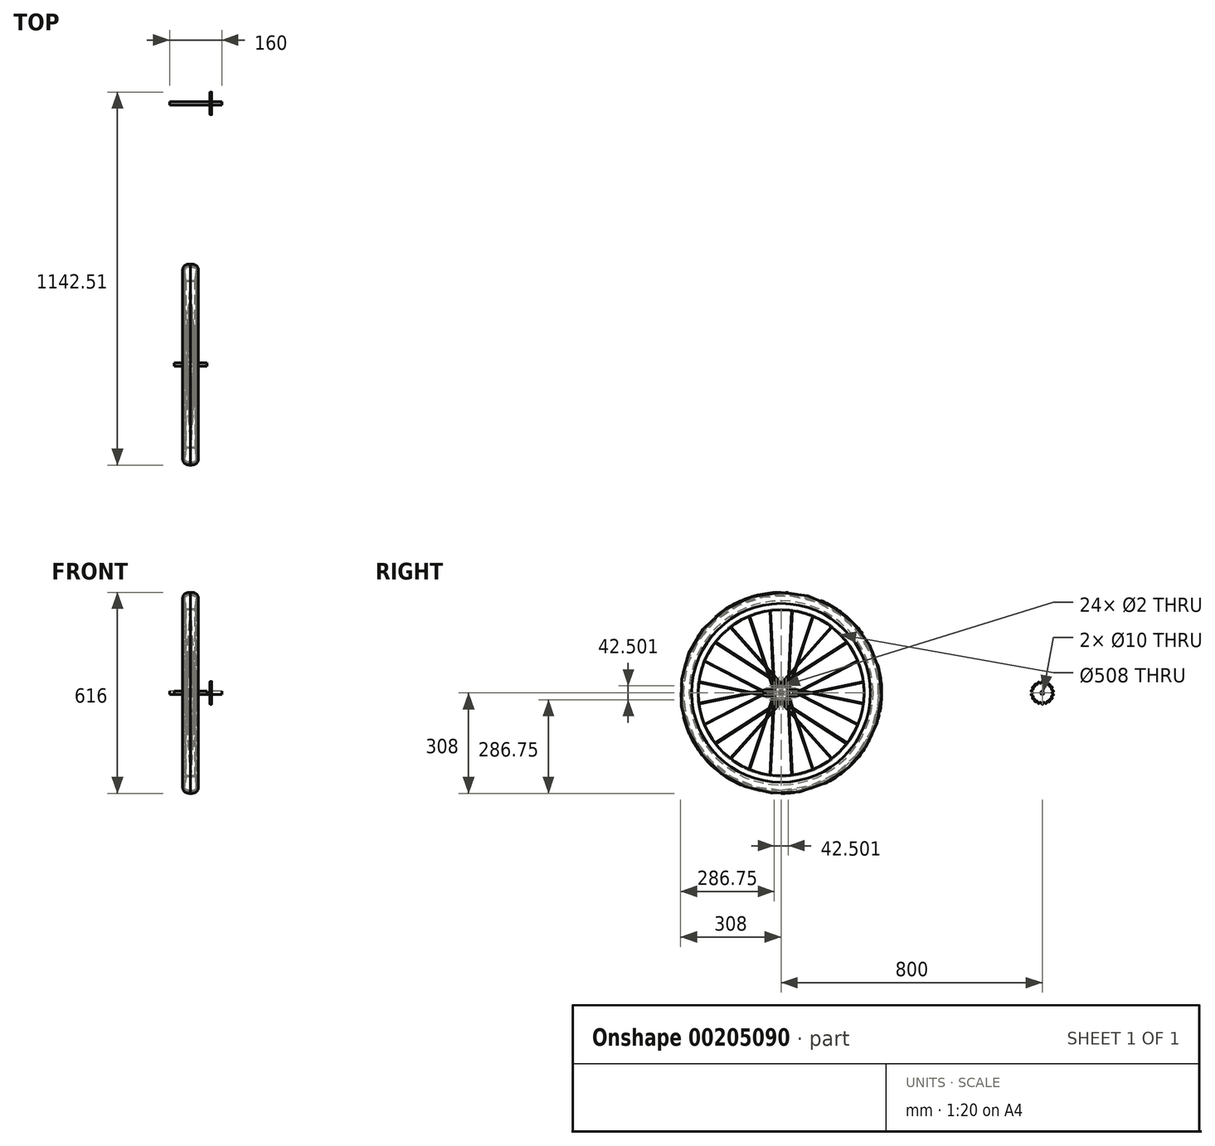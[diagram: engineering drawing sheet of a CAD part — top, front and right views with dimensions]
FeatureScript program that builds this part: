
annotation { "Feature Type Name" : "Feature", "Feature Type Description" : "" }
export const myFeature = defineFeature(function(context is Context, id is Id, definition is map)
    precondition{}
    {
        {
            var Q0;
            Q0=qCreatedBy(makeId("Right.planeOp"),FACE);
            var sketch = newSketch(context, id + "F0", { "sketchPlane" : qUnion([Q0])});
            skCircle(sketch, "E0", {"center": v(0, 0) * mm, "radius": 8 * mm});
            skCircle(sketch, "E1", {"center": v(0, 0) * mm, "radius": 5 * mm});
            skSolve(sketch);
        }
        {
            var Q0;
            Q0 = qSketchRegion(id + "F0", true);
            extrude(context, id + "F1", {"entities" : qUnion([Q0]), "depth" : 15 * mm});
        }
        {
            var Q0;
            Q0=makeQuery(id+"F1.opExtrude","CAP_FACE",FACE,{"disambiguationData":[OSD([sQuery(id+"F0.wireOp",EDGE,"E0"),sQuery(id+"F0.wireOp",EDGE,"E1")])],"isStart":false});
            var sketch = newSketch(context, id + "F2", { "sketchPlane" : qUnion([Q0])});
            skCircle(sketch, "E2", {"center": v(0, 0) * mm, "radius": 25 * mm});
            skCircle(sketch, "E3", {"center": v(0, 0) * mm, "radius": 5 * mm});
            skSolve(sketch);
        }
        {
            var Q0;
            Q0 = qSketchRegion(id + "F2", true);
            extrude(context, id + "F3", {"entities" : qUnion([Q0]), "operationType" : NewBodyOperationType.ADD, "oppositeDirection" : true, "depth" : 2 * mm});
        }
        {
            var Q0;
            Q0=makeQuery(id+"F3.boolean.opBoolean","MERGE",FACE,{"derivedFrom":[makeQuery(id+"F1.opExtrude","CAP_FACE",FACE,{"disambiguationData":[OSD([sQuery(id+"F0.wireOp",EDGE,"E0"),sQuery(id+"F0.wireOp",EDGE,"E1")])],"isStart":false}),makeQuery(id+"F3.opExtrude","CAP_FACE",FACE,{"disambiguationData":[OSD([sQuery(id+"F2.wireOp",EDGE,"E2"),sQuery(id+"F2.wireOp",EDGE,"E3")])],"isStart":true})]});
            var sketch = newSketch(context, id + "F4", { "sketchPlane" : qUnion([Q0])});
            skCircle(sketch, "E4", {"center": v(5.7, 21.25) * mm, "radius": 1 * mm});
            skLineSegment(sketch, "E5", {"start": v(0, 0) * mm, "end": v(5.7, 21.25) * mm, "construction": true});
            skCircle(sketch, "E6.1.0", {"center": v(-5.7, 21.25) * mm, "radius": 1 * mm});
            skCircle(sketch, "E6.2.0", {"center": v(-15.56, 15.56) * mm, "radius": 1 * mm});
            skCircle(sketch, "E6.3.0", {"center": v(-21.25, 5.7) * mm, "radius": 1 * mm});
            skCircle(sketch, "E6.4.0", {"center": v(-21.25, -5.7) * mm, "radius": 1 * mm});
            skCircle(sketch, "E6.5.0", {"center": v(-15.56, -15.56) * mm, "radius": 1 * mm});
            skCircle(sketch, "E6.6.0", {"center": v(-5.7, -21.25) * mm, "radius": 1 * mm});
            skCircle(sketch, "E6.7.0", {"center": v(5.7, -21.25) * mm, "radius": 1 * mm});
            skCircle(sketch, "E6.8.0", {"center": v(15.56, -15.56) * mm, "radius": 1 * mm});
            skCircle(sketch, "E6.9.0", {"center": v(21.25, -5.7) * mm, "radius": 1 * mm});
            skCircle(sketch, "E6.10.0", {"center": v(21.25, 5.7) * mm, "radius": 1 * mm});
            skCircle(sketch, "E6.11.0", {"center": v(15.56, 15.56) * mm, "radius": 1 * mm});
            skPoint(sketch, "E6.center", {"position": v(0, 0) * mm});
            skSolve(sketch);
        }
        {
            var Q0;
            Q0 = qSketchRegion(id + "F4", true);
            extrude(context, id + "F5", {"entities" : qUnion([Q0]), "operationType" : NewBodyOperationType.REMOVE, "endBound" : BoundingType.THROUGH_ALL, "oppositeDirection" : true, "depth" : 25 * mm});
        }
        {
            var Q0;
            Q0=makeQuery(id+"F1.opExtrude","SWEPT_BODY",BODY,{"disambiguationData":[OSD([sQuery(id+"F0.wireOp",EDGE,"E0"),sQuery(id+"F0.wireOp",EDGE,"E1")])]});
            var Q1;
            Q1=makeQuery(id+"F1.opExtrude","CAP_FACE",FACE,{"disambiguationData":[OSD([sQuery(id+"F0.wireOp",EDGE,"E0"),sQuery(id+"F0.wireOp",EDGE,"E1")])],"isStart":true});
            mirror(context, id + "F6", {"operationType" : NewBodyOperationType.ADD, "entities" : qUnion([Q0]), "mirrorPlane" : qUnion([Q1])});
        }
        {
            var Q0;
            Q0=qCreatedBy(makeId("Front.planeOp"),FACE);
            var sketch = newSketch(context, id + "F7", { "sketchPlane" : qUnion([Q0])});
            skLineSegment(sketch, "E7", {"start": v(0, 254) * mm, "end": v(20, 254) * mm});
            skLineSegment(sketch, "E8", {"start": v(20, 254) * mm, "end": v(21.74, 273.92) * mm});
            skLineSegment(sketch, "E9", {"start": v(21.74, 273.92) * mm, "end": v(18.75, 274.19) * mm});
            skLineSegment(sketch, "E10", {"start": v(18.75, 274.19) * mm, "end": v(17.25, 257) * mm});
            skLineSegment(sketch, "E11", {"start": v(17.25, 257) * mm, "end": v(0, 257) * mm});
            skLineSegment(sketch, "E12", {"start": v(0, 257) * mm, "end": v(0, 254) * mm, "construction": true});
            skLineSegment(sketch, "E13.MirrorCS", {"start": v(0, 254) * mm, "end": v(-20, 254) * mm});
            skLineSegment(sketch, "E14.MirrorCS", {"start": v(-20, 254) * mm, "end": v(-21.74, 273.92) * mm});
            skLineSegment(sketch, "E15.MirrorCS", {"start": v(-21.74, 273.92) * mm, "end": v(-18.75, 274.19) * mm});
            skLineSegment(sketch, "E16.MirrorCS", {"start": v(-18.75, 274.19) * mm, "end": v(-17.25, 257) * mm});
            skLineSegment(sketch, "E17.MirrorCS", {"start": v(-17.25, 257) * mm, "end": v(0, 257) * mm});
            skSolve(sketch);
        }
        {
            var Q0;
            Q0 = qSketchRegion(id + "F7", true);
            var Q1;
            Q1=makeQuery(id+"F3.opExtrude","CAP_EDGE",EDGE,{"disambiguationData":[OSD([sQuery(id+"F2.wireOp",EDGE,"E2")])],"isStart":false});
            revolve(context, id + "F8", {"entities" : qUnion([Q0]), "axis" : qUnion([Q1]), "revolveType" : RevolveType.FULL});
        }
        {
            var Q0;
            Q0=qCreatedBy(makeId("Right.planeOp"),FACE);
            var sketch = newSketch(context, id + "F9", { "sketchPlane" : qUnion([Q0])});
            skPoint(sketch, "E18", {"position": v(33.28, 252.82) * mm});
            skPoint(sketch, "E19.1.0", {"position": v(-33.28, 252.82) * mm});
            skPoint(sketch, "E19.2.0", {"position": v(-97.58, 235.59) * mm});
            skPoint(sketch, "E19.3.0", {"position": v(-155.23, 202.3) * mm});
            skPoint(sketch, "E19.4.0", {"position": v(-202.3, 155.23) * mm});
            skPoint(sketch, "E19.5.0", {"position": v(-235.59, 97.58) * mm});
            skPoint(sketch, "E19.6.0", {"position": v(-252.82, 33.28) * mm});
            skPoint(sketch, "E19.7.0", {"position": v(-252.82, -33.28) * mm});
            skPoint(sketch, "E19.8.0", {"position": v(-235.59, -97.58) * mm});
            skPoint(sketch, "E19.9.0", {"position": v(-202.3, -155.23) * mm});
            skPoint(sketch, "E19.10.0", {"position": v(-155.23, -202.3) * mm});
            skPoint(sketch, "E19.11.0", {"position": v(-97.58, -235.59) * mm});
            skPoint(sketch, "E19.12.0", {"position": v(-33.28, -252.82) * mm});
            skPoint(sketch, "E19.13.0", {"position": v(33.28, -252.82) * mm});
            skPoint(sketch, "E19.14.0", {"position": v(97.58, -235.59) * mm});
            skPoint(sketch, "E19.15.0", {"position": v(155.23, -202.3) * mm});
            skPoint(sketch, "E19.16.0", {"position": v(202.3, -155.23) * mm});
            skPoint(sketch, "E19.17.0", {"position": v(235.59, -97.58) * mm});
            skPoint(sketch, "E19.18.0", {"position": v(252.82, -33.28) * mm});
            skPoint(sketch, "E19.19.0", {"position": v(252.82, 33.28) * mm});
            skPoint(sketch, "E19.20.0", {"position": v(235.59, 97.58) * mm});
            skPoint(sketch, "E19.21.0", {"position": v(202.3, 155.23) * mm});
            skPoint(sketch, "E19.22.0", {"position": v(155.23, 202.3) * mm});
            skPoint(sketch, "E19.23.0", {"position": v(97.58, 235.59) * mm});
            skPoint(sketch, "E19.center", {"position": v(0, 0) * mm});
            skLineSegment(sketch, "E20", {"start": v(-33.28, 252.82) * mm, "end": v(-21.25, 5.7) * mm, "construction": true});
            skLineSegment(sketch, "E21", {"start": v(0, 0) * mm, "end": v(3.26, 24.79) * mm, "construction": true});
            skLineSegment(sketch, "E22", {"start": v(-15.56, 15.56) * mm, "end": v(-252.82, -33.28) * mm, "construction": true});
            skLineSegment(sketch, "E23", {"start": v(-21.25, 5.7) * mm, "end": v(-97.58, 235.59) * mm, "construction": true});
            skLineSegment(sketch, "E24", {"start": v(-15.56, 15.56) * mm, "end": v(-235.59, -97.58) * mm, "construction": true});
            skLineSegment(sketch, "E25.1.0", {"start": v(-235.59, 97.58) * mm, "end": v(-15.56, -15.56) * mm, "construction": true});
            skLineSegment(sketch, "E25.1.1", {"start": v(-15.56, -15.56) * mm, "end": v(-252.82, 33.28) * mm, "construction": true});
            skLineSegment(sketch, "E25.1.2", {"start": v(-21.25, -5.7) * mm, "end": v(-97.58, -235.59) * mm, "construction": true});
            skLineSegment(sketch, "E25.1.3", {"start": v(-21.25, -5.7) * mm, "end": v(-33.28, -252.82) * mm, "construction": true});
            skLineSegment(sketch, "E25.2.0", {"start": v(-202.3, -155.23) * mm, "end": v(5.7, -21.25) * mm, "construction": true});
            skLineSegment(sketch, "E25.2.1", {"start": v(5.7, -21.25) * mm, "end": v(-155.23, -202.3) * mm, "construction": true});
            skLineSegment(sketch, "E25.2.2", {"start": v(-5.7, -21.25) * mm, "end": v(155.23, -202.3) * mm, "construction": true});
            skLineSegment(sketch, "E25.2.3", {"start": v(-5.7, -21.25) * mm, "end": v(202.3, -155.23) * mm, "construction": true});
            skLineSegment(sketch, "E25.3.0", {"start": v(33.28, -252.82) * mm, "end": v(21.25, -5.7) * mm, "construction": true});
            skLineSegment(sketch, "E25.3.1", {"start": v(21.25, -5.7) * mm, "end": v(97.58, -235.59) * mm, "construction": true});
            skLineSegment(sketch, "E25.3.2", {"start": v(15.56, -15.56) * mm, "end": v(252.82, 33.28) * mm, "construction": true});
            skLineSegment(sketch, "E25.3.3", {"start": v(15.56, -15.56) * mm, "end": v(235.59, 97.58) * mm, "construction": true});
            skLineSegment(sketch, "E25.4.0", {"start": v(235.59, -97.58) * mm, "end": v(15.56, 15.56) * mm, "construction": true});
            skLineSegment(sketch, "E25.4.1", {"start": v(15.56, 15.56) * mm, "end": v(252.82, -33.28) * mm, "construction": true});
            skLineSegment(sketch, "E25.4.2", {"start": v(21.25, 5.7) * mm, "end": v(97.58, 235.59) * mm, "construction": true});
            skLineSegment(sketch, "E25.4.3", {"start": v(21.25, 5.7) * mm, "end": v(33.28, 252.82) * mm, "construction": true});
            skLineSegment(sketch, "E25.5.0", {"start": v(202.3, 155.23) * mm, "end": v(-5.7, 21.25) * mm, "construction": true});
            skLineSegment(sketch, "E25.5.1", {"start": v(-5.7, 21.25) * mm, "end": v(155.23, 202.3) * mm, "construction": true});
            skLineSegment(sketch, "E25.5.2", {"start": v(5.7, 21.25) * mm, "end": v(-155.23, 202.3) * mm, "construction": true});
            skLineSegment(sketch, "E25.5.3", {"start": v(5.7, 21.25) * mm, "end": v(-202.3, 155.23) * mm, "construction": true});
            skSolve(sketch);
        }
        {
            var Q0;
            Q0=sQuery(id+"F9.wireOp",EDGE,"E20");
            cPlane(context, id + "F10", {"entities" : qUnion([Q0]), "cplaneType" : CPlaneType.LINE_ANGLE, "offset" : 25 * mm, "angle" : 90 * degree, "width" : 150 * mm, "height" : 150 * mm});
        }
        {
            var Q0;
            Q0=qCreatedBy(id+"F10.planeOp",FACE);
            var sketch = newSketch(context, id + "F11", { "sketchPlane" : qUnion([Q0])});
            skLineSegment(sketch, "E26", {"start": v(0, 254.14) * mm, "end": v(-17.5, 8.33) * mm});
            skLineSegment(sketch, "E27", {"start": v(-12, 6.72) * mm, "end": v(-16, 6.72) * mm});
            skArc(sketch, "E28", {"start": v(-16, 6.72) * mm, "mid": v(-17.1, 7.2) * mm, "end": v(-17.5, 8.33) * mm});
            skSolve(sketch);
        }
        {
            var Q0;
            Q0=sQuery(id+"F11.wireOp",VERTEX,"E27.start");
            var Q1;
            Q1=sQuery(id+"F11.wireOp",EDGE,"E27");
            cPlane(context, id + "F12", {"entities" : qUnion([Q0, Q1]), "cplaneType" : CPlaneType.CURVE_POINT, "offset" : 25 * mm, "width" : 150 * mm, "height" : 150 * mm});
        }
        {
            var Q0;
            Q0=qCreatedBy(id+"F12.planeOp",FACE);
            var sketch = newSketch(context, id + "F13", { "sketchPlane" : qUnion([Q0])});
            skCircle(sketch, "E29", {"center": v(-21.25, 5.7) * mm, "radius": 1 * mm});
            skSolve(sketch);
        }
        {
            var Q0;
            Q0=makeQuery(id+"F13.imprint","IMPRINT",FACE,{"disambiguationData":[TD([[makeQuery(id+"F13.imprint","IMPRINT",EDGE,{"derivedFrom":sQuery(id+"F13.wireOp",EDGE,"E29")}),1.0]])]});
            var Q1;
            Q1=sQuery(id+"F11.wireOp",EDGE,"E28");
            var Q2;
            Q2=sQuery(id+"F11.wireOp",EDGE,"E27");
            var Q3;
            Q3=sQuery(id+"F11.wireOp",EDGE,"E26");
            sweep(context, id + "F14", {"profiles" : qUnion([Q0]), "path" : qUnion([Q1, Q2, Q3])});
        }
        {
            var Q0;
            Q0=sQuery(id+"F9.wireOp",EDGE,"E22");
            cPlane(context, id + "F15", {"entities" : qUnion([Q0]), "cplaneType" : CPlaneType.LINE_ANGLE, "offset" : 25 * mm, "angle" : 0 * degree, "width" : 150 * mm, "height" : 150 * mm});
        }
        {
            var Q0;
            Q0=qCreatedBy(id+"F15.planeOp",FACE);
            var sketch = newSketch(context, id + "F16", { "sketchPlane" : qUnion([Q0])});
            skLineSegment(sketch, "E30", {"start": v(0, 254.34) * mm, "end": v(10, 13.54) * mm});
            skLineSegment(sketch, "E31", {"start": v(11.5, 12.1) * mm, "end": v(16, 12.1) * mm});
            skArc(sketch, "E32", {"start": v(11.5, 12.1) * mm, "mid": v(10.46, 12.52) * mm, "end": v(10, 13.54) * mm});
            skSolve(sketch);
        }
        {
            var Q0;
            Q0=sQuery(id+"F16.wireOp",EDGE,"E31");
            var Q1;
            Q1=sQuery(id+"F16.wireOp",VERTEX,"E31.end");
            cPlane(context, id + "F17", {"entities" : qUnion([Q0, Q1]), "cplaneType" : CPlaneType.CURVE_POINT, "offset" : 25 * mm, "width" : 150 * mm, "height" : 150 * mm});
        }
        {
            var Q0;
            Q0=qCreatedBy(id+"F17.planeOp",FACE);
            var sketch = newSketch(context, id + "F18", { "sketchPlane" : qUnion([Q0])});
            skCircle(sketch, "E33", {"center": v(-15.56, 15.56) * mm, "radius": 1 * mm});
            skSolve(sketch);
        }
        {
            var Q0;
            Q0=makeQuery(id+"F18.imprint","IMPRINT",FACE,{"disambiguationData":[TD([[makeQuery(id+"F18.imprint","IMPRINT",EDGE,{"derivedFrom":sQuery(id+"F18.wireOp",EDGE,"E33")}),1.0]])]});
            var Q1;
            Q1=sQuery(id+"F16.wireOp",EDGE,"E31");
            var Q2;
            Q2=sQuery(id+"F16.wireOp",EDGE,"E32");
            var Q3;
            Q3=sQuery(id+"F16.wireOp",EDGE,"E30");
            sweep(context, id + "F19", {"profiles" : qUnion([Q0]), "path" : qUnion([Q1, Q2, Q3])});
        }
        {
            var Q0;
            Q0=makeQuery(id+"F14.opSweep","SWEPT_BODY",BODY,{"disambiguationData":[OSD([sQuery(id+"F11.wireOp",EDGE,"E27"),sQuery(id+"F13.wireOp",EDGE,"E29")])]});
            var Q1;
            Q1=makeQuery(id+"F19.opSweep","SWEPT_BODY",BODY,{"disambiguationData":[OSD([sQuery(id+"F16.wireOp",EDGE,"E30"),sQuery(id+"F18.wireOp",EDGE,"E33")])]});
            var Q2;
            Q2=makeQuery(id+"F3.opExtrude","CAP_EDGE",EDGE,{"disambiguationData":[OSD([sQuery(id+"F2.wireOp",EDGE,"E2")])],"isStart":true});
            circularPattern(context, id + "F20", {"entities" : qUnion([Q0, Q1]), "axis" : qUnion([Q2]), "angle" : 360 * degree, "instanceCount" : 6, "equalSpace" : true});
        }
        {
            var Q0;
            Q0=qCreatedBy(makeId("Right.planeOp"),FACE);
            var sketch = newSketch(context, id + "F21", { "sketchPlane" : qUnion([Q0])});
            skLineSegment(sketch, "E34", {"start": v(0, 0) * mm, "end": v(0, 5) * mm, "construction": true});
            skSolve(sketch);
        }
        {
            var Q0;
            Q0=makeQuery(id+"F14.opSweep","SWEPT_BODY",BODY,{"disambiguationData":[OSD([sQuery(id+"F11.wireOp",EDGE,"E27"),sQuery(id+"F13.wireOp",EDGE,"E29")])]});
            var Q1;
            Q1=makeQuery(id+"F19.opSweep","SWEPT_BODY",BODY,{"disambiguationData":[OSD([sQuery(id+"F16.wireOp",EDGE,"E30"),sQuery(id+"F18.wireOp",EDGE,"E33")])]});
            var Q2;
            Q2=makeQuery(id+"F20.opPattern","COPY",BODY,{"derivedFrom":makeQuery(id+"F14.opSweep","SWEPT_BODY",BODY,{"disambiguationData":[OSD([sQuery(id+"F11.wireOp",EDGE,"E27"),sQuery(id+"F13.wireOp",EDGE,"E29")])]}),"instanceName":"1"});
            var Q3;
            Q3=makeQuery(id+"F20.opPattern","COPY",BODY,{"derivedFrom":makeQuery(id+"F19.opSweep","SWEPT_BODY",BODY,{"disambiguationData":[OSD([sQuery(id+"F16.wireOp",EDGE,"E30"),sQuery(id+"F18.wireOp",EDGE,"E33")])]}),"instanceName":"1"});
            var Q4;
            Q4=makeQuery(id+"F20.opPattern","COPY",BODY,{"derivedFrom":makeQuery(id+"F14.opSweep","SWEPT_BODY",BODY,{"disambiguationData":[OSD([sQuery(id+"F11.wireOp",EDGE,"E27"),sQuery(id+"F13.wireOp",EDGE,"E29")])]}),"instanceName":"2"});
            var Q5;
            Q5=makeQuery(id+"F20.opPattern","COPY",BODY,{"derivedFrom":makeQuery(id+"F19.opSweep","SWEPT_BODY",BODY,{"disambiguationData":[OSD([sQuery(id+"F16.wireOp",EDGE,"E30"),sQuery(id+"F18.wireOp",EDGE,"E33")])]}),"instanceName":"2"});
            var Q6;
            Q6=makeQuery(id+"F20.opPattern","COPY",BODY,{"derivedFrom":makeQuery(id+"F14.opSweep","SWEPT_BODY",BODY,{"disambiguationData":[OSD([sQuery(id+"F11.wireOp",EDGE,"E27"),sQuery(id+"F13.wireOp",EDGE,"E29")])]}),"instanceName":"3"});
            var Q7;
            Q7=makeQuery(id+"F20.opPattern","COPY",BODY,{"derivedFrom":makeQuery(id+"F19.opSweep","SWEPT_BODY",BODY,{"disambiguationData":[OSD([sQuery(id+"F16.wireOp",EDGE,"E30"),sQuery(id+"F18.wireOp",EDGE,"E33")])]}),"instanceName":"3"});
            var Q8;
            Q8=makeQuery(id+"F20.opPattern","COPY",BODY,{"derivedFrom":makeQuery(id+"F14.opSweep","SWEPT_BODY",BODY,{"disambiguationData":[OSD([sQuery(id+"F11.wireOp",EDGE,"E27"),sQuery(id+"F13.wireOp",EDGE,"E29")])]}),"instanceName":"4"});
            var Q9;
            Q9=makeQuery(id+"F20.opPattern","COPY",BODY,{"derivedFrom":makeQuery(id+"F19.opSweep","SWEPT_BODY",BODY,{"disambiguationData":[OSD([sQuery(id+"F16.wireOp",EDGE,"E30"),sQuery(id+"F18.wireOp",EDGE,"E33")])]}),"instanceName":"4"});
            var Q10;
            Q10=makeQuery(id+"F20.opPattern","COPY",BODY,{"derivedFrom":makeQuery(id+"F14.opSweep","SWEPT_BODY",BODY,{"disambiguationData":[OSD([sQuery(id+"F11.wireOp",EDGE,"E27"),sQuery(id+"F13.wireOp",EDGE,"E29")])]}),"instanceName":"5"});
            var Q11;
            Q11=makeQuery(id+"F20.opPattern","COPY",BODY,{"derivedFrom":makeQuery(id+"F19.opSweep","SWEPT_BODY",BODY,{"disambiguationData":[OSD([sQuery(id+"F16.wireOp",EDGE,"E30"),sQuery(id+"F18.wireOp",EDGE,"E33")])]}),"instanceName":"5"});
            var Q12;
            Q12=sQuery(id+"F21.wireOp",EDGE,"E34");
            circularPattern(context, id + "F22", {"entities" : qUnion([Q0, Q1, Q2, Q3, Q4, Q5, Q6, Q7, Q8, Q9, Q10, Q11]), "axis" : qUnion([Q12]), "angle" : 360 * degree, "instanceCount" : 2, "equalSpace" : true});
        }
        {
            var Q0;
            Q0=qCreatedBy(makeId("Right.planeOp"),FACE);
            var sketch = newSketch(context, id + "F23", { "sketchPlane" : qUnion([Q0])});
            skCircle(sketch, "E35.0", {"center": v(0, 0) * mm, "radius": 5 * mm});
            skSolve(sketch);
        }
        {
            var Q0;
            Q0 = qSketchRegion(id + "F23", true);
            extrude(context, id + "F24", {"entities" : qUnion([Q0]), "depth" : 50 * mm, "hasSecondDirection" : true, "secondDirectionOppositeDirection" : true, "secondDirectionDepth" : 50 * mm});
        }
        {
            var Q0;
            Q0=qCreatedBy(makeId("Front.planeOp"),FACE);
            var sketch = newSketch(context, id + "F25", { "sketchPlane" : qUnion([Q0])});
            skFitSpline(sketch, "E36", {"points": [v(0, 302) * mm, v(-18, 296) * mm, v(-21, 286) * mm, v(-18.75, 274.19) * mm], "startDerivative": vector(-76.14, 0) * mm, "endDerivative": vector(3.33, -38.1) * mm});
            skFitSpline(sketch, "E37.MirrorCS", {"points": [v(0, 302) * mm, v(18, 296) * mm, v(21, 286) * mm, v(18.75, 274.19) * mm], "startDerivative": vector(76.14, 0) * mm, "endDerivative": vector(-3.33, -38.1) * mm});
            skLineSegment(sketch, "E38", {"start": v(-18.75, 274.19) * mm, "end": v(-17.25, 257) * mm});
            skLineSegment(sketch, "E39.MirrorCS", {"start": v(18.75, 274.19) * mm, "end": v(17.25, 257) * mm});
            skLineSegment(sketch, "E40.0", {"start": v(-15.77, 274.45) * mm, "end": v(-14.24, 257) * mm});
            skFitSpline(sketch, "E40.1", {"points": [v(0, 299) * mm, v(-3.03, 299) * mm, v(-6.77, 298.67) * mm, v(-10.38, 297.74) * mm, v(-12.47, 296.84) * mm, v(-14.08, 295.8) * mm, v(-15.34, 294.59) * mm, v(-16.38, 293.17) * mm, v(-17.18, 291.58) * mm, v(-17.64, 290.14) * mm, v(-17.88, 288.94) * mm, v(-18, 288.02) * mm, v(-18.03, 287.24) * mm, v(-18.03, 286.61) * mm, v(-18, 285.99) * mm, v(-17.92, 285.18) * mm, v(-17.76, 284.16) * mm, v(-17.55, 283.1) * mm, v(-17.2, 281.61) * mm, v(-16.7, 279.66) * mm, v(-16.12, 277.16) * mm, v(-15.85, 275.37) * mm, v(-15.77, 274.45) * mm]});
            skFitSpline(sketch, "E40.2", {"points": [v(0, 299) * mm, v(3.03, 299) * mm, v(6.77, 298.67) * mm, v(10.38, 297.74) * mm, v(12.47, 296.84) * mm, v(14.08, 295.8) * mm, v(15.34, 294.59) * mm, v(16.38, 293.17) * mm, v(17.18, 291.58) * mm, v(17.64, 290.14) * mm, v(17.88, 288.94) * mm, v(18, 288.02) * mm, v(18.03, 287.24) * mm, v(18.03, 286.61) * mm, v(18, 285.99) * mm, v(17.92, 285.18) * mm, v(17.76, 284.16) * mm, v(17.55, 283.1) * mm, v(17.2, 281.61) * mm, v(16.7, 279.66) * mm, v(16.12, 277.16) * mm, v(15.85, 275.37) * mm, v(15.77, 274.45) * mm]});
            skLineSegment(sketch, "E40.3", {"start": v(15.77, 274.45) * mm, "end": v(14.24, 257) * mm});
            skLineSegment(sketch, "E41", {"start": v(-17.25, 257) * mm, "end": v(-14.24, 257) * mm});
            skLineSegment(sketch, "E42", {"start": v(17.25, 257) * mm, "end": v(14.24, 257) * mm});
            skSolve(sketch);
        }
        {
            var Q0;
            Q0 = qSketchRegion(id + "F25", true);
            var Q1;
            Q1=makeQuery(id+"F8.opRevolve","SWEPT_EDGE",EDGE,{"disambiguationData":[OSD([sQuery(id+"F7.wireOp",EDGE,"E14.MirrorCS"),sQuery(id+"F7.wireOp",EDGE,"E15.MirrorCS")])]});
            revolve(context, id + "F26", {"entities" : qUnion([Q0]), "axis" : qUnion([Q1]), "revolveType" : RevolveType.FULL});
        }
        {
            var Q0;
            Q0=qCreatedBy(makeId("Front.planeOp"),FACE);
            var sketch = newSketch(context, id + "F27", { "sketchPlane" : qUnion([Q0])});
            skFitSpline(sketch, "E43.0", {"points": [v(0, 308) * mm, v(-1.72, 308) * mm, v(-4.92, 307.86) * mm, v(-9.07, 307.26) * mm, v(-12.64, 306.27) * mm, v(-15.68, 304.9) * mm, v(-17.8, 303.44) * mm, v(-19.24, 302.13) * mm, v(-20.2, 301.08) * mm, v(-21.04, 299.98) * mm, v(-22.04, 298.42) * mm, v(-23.01, 296.32) * mm, v(-23.62, 294.05) * mm, v(-23.9, 292.16) * mm, v(-24, 290.7) * mm, v(-24.02, 289.2) * mm, v(-23.92, 287.15) * mm, v(-23.6, 284.59) * mm, v(-23.07, 281.55) * mm, v(-22.5, 278.65) * mm, v(-22, 276.02) * mm, v(-21.8, 274.55) * mm, v(-21.74, 273.92) * mm]});
            skFitSpline(sketch, "E43.1", {"points": [v(0, 308) * mm, v(1.72, 308) * mm, v(4.92, 307.86) * mm, v(9.07, 307.26) * mm, v(12.64, 306.27) * mm, v(15.68, 304.9) * mm, v(17.8, 303.44) * mm, v(19.24, 302.13) * mm, v(20.2, 301.08) * mm, v(21.04, 299.98) * mm, v(22.04, 298.42) * mm, v(23.01, 296.32) * mm, v(23.62, 294.05) * mm, v(23.9, 292.16) * mm, v(24, 290.7) * mm, v(24.02, 289.2) * mm, v(23.92, 287.15) * mm, v(23.6, 284.59) * mm, v(23.07, 281.55) * mm, v(22.5, 278.65) * mm, v(22, 276.02) * mm, v(21.8, 274.55) * mm, v(21.74, 273.92) * mm]});
            skFitSpline(sketch, "E44.0", {"points": [v(0, 305) * mm, v(-10, 305) * mm, v(-18.86, 300.78) * mm, v(-22.3, 289.12) * mm, v(-19.1, 278.17) * mm, v(-18.75, 274.19) * mm]});
            skFitSpline(sketch, "E45.0", {"points": [v(0, 305) * mm, v(10, 305) * mm, v(18.86, 300.78) * mm, v(22.3, 289.12) * mm, v(19.1, 278.17) * mm, v(18.75, 274.19) * mm]});
            skLineSegment(sketch, "E46", {"start": v(-21.74, 273.92) * mm, "end": v(-18.75, 274.19) * mm});
            skLineSegment(sketch, "E47", {"start": v(18.75, 274.19) * mm, "end": v(21.74, 273.92) * mm});
            skSolve(sketch);
        }
        {
            var Q0;
            Q0 = qSketchRegion(id + "F27", true);
            var Q1;
            Q1=makeQuery(id+"F8.opRevolve","SWEPT_EDGE",EDGE,{"disambiguationData":[OSD([sQuery(id+"F7.wireOp",EDGE,"E8"),sQuery(id+"F7.wireOp",EDGE,"E9")])]});
            revolve(context, id + "F28", {"operationType" : NewBodyOperationType.ADD, "entities" : qUnion([Q0]), "axis" : qUnion([Q1]), "revolveType" : RevolveType.FULL});
        }
        {
            var Q0;
            Q0=qCreatedBy(id+"F17.planeOp",FACE);
            var sketch = newSketch(context, id + "F29", { "sketchPlane" : qUnion([Q0])});
            skCircle(sketch, "E48", {"center": v(800, 0) * mm, "radius": 5 * mm});
            skSolve(sketch);
        }
        {
            var Q0;
            Q0 = qSketchRegion(id + "F29", true);
            extrude(context, id + "F30", {"entities" : qUnion([Q0]), "depth" : 80 * mm, "hasSecondDirection" : true, "secondDirectionOppositeDirection" : true, "secondDirectionDepth" : 80 * mm});
        }
        {
            var Q0;
            Q0=qCreatedBy(makeId("Right.planeOp"),FACE);
            cPlane(context, id + "F31", {"entities" : qUnion([Q0]), "cplaneType" : CPlaneType.OFFSET, "offset" : 60 * mm, "width" : 150 * mm, "height" : 150 * mm});
        }
        {
            var Q0;
            Q0=qCreatedBy(id+"F31.planeOp",FACE);
            var sketch = newSketch(context, id + "F32", { "sketchPlane" : qUnion([Q0])});
            skCircle(sketch, "E49.0", {"center": v(800, 0) * mm, "radius": 5 * mm});
            skCircle(sketch, "E50", {"center": v(800, 0) * mm, "radius": 30 * mm});
            skLineSegment(sketch, "E51", {"start": v(800, 0) * mm, "end": v(800, 30) * mm, "construction": true});
            skArc(sketch, "E52", {"start": v(802.5, 32.5) * mm, "mid": v(803.2, 30.6) * mm, "end": v(804.97, 29.59) * mm});
            skArc(sketch, "E53", {"start": v(802.5, 32.5) * mm, "mid": v(801.77, 34.27) * mm, "end": v(800, 35) * mm});
            skArc(sketch, "E54.MirrorCS", {"start": v(797.5, 32.5) * mm, "mid": v(798.23, 34.27) * mm, "end": v(800, 35) * mm});
            skArc(sketch, "E55.MirrorCS", {"start": v(797.5, 32.5) * mm, "mid": v(796.8, 30.6) * mm, "end": v(795.03, 29.59) * mm});
            skArc(sketch, "E56.1.0", {"start": v(791.23, 31.4) * mm, "mid": v(789.94, 32.8) * mm, "end": v(788.03, 32.89) * mm});
            skArc(sketch, "E56.1.1", {"start": v(786.54, 29.68) * mm, "mid": v(786.62, 31.6) * mm, "end": v(788.03, 32.89) * mm});
            skArc(sketch, "E56.1.2", {"start": v(786.54, 29.68) * mm, "mid": v(786.53, 27.65) * mm, "end": v(785.21, 26.1) * mm});
            skArc(sketch, "E56.1.3", {"start": v(791.23, 31.4) * mm, "mid": v(792.54, 29.84) * mm, "end": v(794.55, 29.5) * mm});
            skArc(sketch, "E56.2.0", {"start": v(781.02, 26.5) * mm, "mid": v(779.33, 27.39) * mm, "end": v(777.5, 26.81) * mm});
            skArc(sketch, "E56.2.1", {"start": v(777.2, 23.29) * mm, "mid": v(776.62, 25.11) * mm, "end": v(777.5, 26.81) * mm});
            skArc(sketch, "E56.2.2", {"start": v(777.2, 23.29) * mm, "mid": v(777.89, 21.38) * mm, "end": v(777.18, 19.47) * mm});
            skArc(sketch, "E56.2.3", {"start": v(781.02, 26.5) * mm, "mid": v(782.79, 25.5) * mm, "end": v(784.79, 25.86) * mm});
            skArc(sketch, "E56.3.0", {"start": v(773.1, 18.42) * mm, "mid": v(771.2, 18.66) * mm, "end": v(769.69, 17.5) * mm});
            skArc(sketch, "E56.3.1", {"start": v(770.6, 14.08) * mm, "mid": v(769.44, 15.6) * mm, "end": v(769.69, 17.5) * mm});
            skArc(sketch, "E56.3.2", {"start": v(770.6, 14.08) * mm, "mid": v(771.9, 12.53) * mm, "end": v(771.9, 10.5) * mm});
            skArc(sketch, "E56.3.3", {"start": v(773.1, 18.42) * mm, "mid": v(775.1, 18.07) * mm, "end": v(776.86, 19.1) * mm});
            skArc(sketch, "E56.4.0", {"start": v(768.43, 8.1) * mm, "mid": v(766.56, 7.7) * mm, "end": v(765.53, 6.08) * mm});
            skArc(sketch, "E56.4.1", {"start": v(767.56, 3.18) * mm, "mid": v(765.95, 4.2) * mm, "end": v(765.53, 6.08) * mm});
            skArc(sketch, "E56.4.2", {"start": v(767.56, 3.18) * mm, "mid": v(769.32, 2.16) * mm, "end": v(770, 0.25) * mm});
            skArc(sketch, "E56.4.3", {"start": v(768.43, 8.1) * mm, "mid": v(770.43, 8.46) * mm, "end": v(771.73, 10.03) * mm});
            skArc(sketch, "E56.5.0", {"start": v(767.56, -3.18) * mm, "mid": v(765.95, -4.2) * mm, "end": v(765.53, -6.08) * mm});
            skArc(sketch, "E56.5.1", {"start": v(768.43, -8.1) * mm, "mid": v(766.56, -7.7) * mm, "end": v(765.53, -6.08) * mm});
            skArc(sketch, "E56.5.2", {"start": v(768.43, -8.1) * mm, "mid": v(770.43, -8.46) * mm, "end": v(771.73, -10.03) * mm});
            skArc(sketch, "E56.5.3", {"start": v(767.56, -3.18) * mm, "mid": v(769.32, -2.16) * mm, "end": v(770, -0.25) * mm});
            skArc(sketch, "E56.6.0", {"start": v(770.6, -14.08) * mm, "mid": v(769.44, -15.6) * mm, "end": v(769.69, -17.5) * mm});
            skArc(sketch, "E56.6.1", {"start": v(773.1, -18.42) * mm, "mid": v(771.2, -18.66) * mm, "end": v(769.69, -17.5) * mm});
            skArc(sketch, "E56.6.2", {"start": v(773.1, -18.42) * mm, "mid": v(775.1, -18.07) * mm, "end": v(776.86, -19.1) * mm});
            skArc(sketch, "E56.6.3", {"start": v(770.6, -14.08) * mm, "mid": v(771.9, -12.53) * mm, "end": v(771.9, -10.5) * mm});
            skArc(sketch, "E56.7.0", {"start": v(777.2, -23.29) * mm, "mid": v(776.62, -25.11) * mm, "end": v(777.5, -26.81) * mm});
            skArc(sketch, "E56.7.1", {"start": v(781.02, -26.5) * mm, "mid": v(779.33, -27.39) * mm, "end": v(777.5, -26.81) * mm});
            skArc(sketch, "E56.7.2", {"start": v(781.02, -26.5) * mm, "mid": v(782.79, -25.5) * mm, "end": v(784.79, -25.86) * mm});
            skArc(sketch, "E56.7.3", {"start": v(777.2, -23.29) * mm, "mid": v(777.89, -21.38) * mm, "end": v(777.18, -19.47) * mm});
            skArc(sketch, "E56.8.0", {"start": v(786.54, -29.68) * mm, "mid": v(786.62, -31.6) * mm, "end": v(788.03, -32.89) * mm});
            skArc(sketch, "E56.8.1", {"start": v(791.23, -31.4) * mm, "mid": v(789.94, -32.8) * mm, "end": v(788.03, -32.89) * mm});
            skArc(sketch, "E56.8.2", {"start": v(791.23, -31.4) * mm, "mid": v(792.54, -29.84) * mm, "end": v(794.55, -29.5) * mm});
            skArc(sketch, "E56.8.3", {"start": v(786.54, -29.68) * mm, "mid": v(786.53, -27.65) * mm, "end": v(785.21, -26.1) * mm});
            skArc(sketch, "E56.9.0", {"start": v(797.5, -32.5) * mm, "mid": v(798.23, -34.27) * mm, "end": v(800, -35) * mm});
            skArc(sketch, "E56.9.1", {"start": v(802.5, -32.5) * mm, "mid": v(801.77, -34.27) * mm, "end": v(800, -35) * mm});
            skArc(sketch, "E56.9.2", {"start": v(802.5, -32.5) * mm, "mid": v(803.2, -30.6) * mm, "end": v(804.97, -29.59) * mm});
            skArc(sketch, "E56.9.3", {"start": v(797.5, -32.5) * mm, "mid": v(796.8, -30.6) * mm, "end": v(795.03, -29.59) * mm});
            skArc(sketch, "E56.10.0", {"start": v(808.77, -31.4) * mm, "mid": v(810.06, -32.8) * mm, "end": v(811.97, -32.89) * mm});
            skArc(sketch, "E56.10.1", {"start": v(813.46, -29.68) * mm, "mid": v(813.38, -31.6) * mm, "end": v(811.97, -32.89) * mm});
            skArc(sketch, "E56.10.2", {"start": v(813.46, -29.68) * mm, "mid": v(813.47, -27.65) * mm, "end": v(814.79, -26.1) * mm});
            skArc(sketch, "E56.10.3", {"start": v(808.77, -31.4) * mm, "mid": v(807.46, -29.84) * mm, "end": v(805.45, -29.5) * mm});
            skArc(sketch, "E56.11.0", {"start": v(818.98, -26.5) * mm, "mid": v(820.67, -27.39) * mm, "end": v(822.5, -26.81) * mm});
            skArc(sketch, "E56.11.1", {"start": v(822.8, -23.29) * mm, "mid": v(823.38, -25.11) * mm, "end": v(822.5, -26.81) * mm});
            skArc(sketch, "E56.11.2", {"start": v(822.8, -23.29) * mm, "mid": v(822.11, -21.38) * mm, "end": v(822.82, -19.47) * mm});
            skArc(sketch, "E56.11.3", {"start": v(818.98, -26.5) * mm, "mid": v(817.21, -25.5) * mm, "end": v(815.21, -25.86) * mm});
            skArc(sketch, "E56.12.0", {"start": v(826.9, -18.42) * mm, "mid": v(828.8, -18.66) * mm, "end": v(830.31, -17.5) * mm});
            skArc(sketch, "E56.12.1", {"start": v(829.4, -14.08) * mm, "mid": v(830.56, -15.6) * mm, "end": v(830.31, -17.5) * mm});
            skArc(sketch, "E56.12.2", {"start": v(829.4, -14.08) * mm, "mid": v(828.1, -12.53) * mm, "end": v(828.1, -10.5) * mm});
            skArc(sketch, "E56.12.3", {"start": v(826.9, -18.42) * mm, "mid": v(824.9, -18.07) * mm, "end": v(823.14, -19.1) * mm});
            skArc(sketch, "E56.13.0", {"start": v(831.57, -8.1) * mm, "mid": v(833.44, -7.7) * mm, "end": v(834.47, -6.08) * mm});
            skArc(sketch, "E56.13.1", {"start": v(832.44, -3.18) * mm, "mid": v(834.05, -4.2) * mm, "end": v(834.47, -6.08) * mm});
            skArc(sketch, "E56.13.2", {"start": v(832.44, -3.18) * mm, "mid": v(830.68, -2.16) * mm, "end": v(830, -0.25) * mm});
            skArc(sketch, "E56.13.3", {"start": v(831.57, -8.1) * mm, "mid": v(829.57, -8.46) * mm, "end": v(828.27, -10.03) * mm});
            skArc(sketch, "E56.14.0", {"start": v(832.44, 3.18) * mm, "mid": v(834.05, 4.2) * mm, "end": v(834.47, 6.08) * mm});
            skArc(sketch, "E56.14.1", {"start": v(831.57, 8.1) * mm, "mid": v(833.44, 7.7) * mm, "end": v(834.47, 6.08) * mm});
            skArc(sketch, "E56.14.2", {"start": v(831.57, 8.1) * mm, "mid": v(829.57, 8.46) * mm, "end": v(828.27, 10.03) * mm});
            skArc(sketch, "E56.14.3", {"start": v(832.44, 3.18) * mm, "mid": v(830.68, 2.16) * mm, "end": v(830, 0.25) * mm});
            skArc(sketch, "E56.15.0", {"start": v(829.4, 14.08) * mm, "mid": v(830.56, 15.6) * mm, "end": v(830.31, 17.5) * mm});
            skArc(sketch, "E56.15.1", {"start": v(826.9, 18.42) * mm, "mid": v(828.8, 18.66) * mm, "end": v(830.31, 17.5) * mm});
            skArc(sketch, "E56.15.2", {"start": v(826.9, 18.42) * mm, "mid": v(824.9, 18.07) * mm, "end": v(823.14, 19.1) * mm});
            skArc(sketch, "E56.15.3", {"start": v(829.4, 14.08) * mm, "mid": v(828.1, 12.53) * mm, "end": v(828.1, 10.5) * mm});
            skArc(sketch, "E56.16.0", {"start": v(822.8, 23.29) * mm, "mid": v(823.38, 25.11) * mm, "end": v(822.5, 26.81) * mm});
            skArc(sketch, "E56.16.1", {"start": v(818.98, 26.5) * mm, "mid": v(820.67, 27.39) * mm, "end": v(822.5, 26.81) * mm});
            skArc(sketch, "E56.16.2", {"start": v(818.98, 26.5) * mm, "mid": v(817.21, 25.5) * mm, "end": v(815.21, 25.86) * mm});
            skArc(sketch, "E56.16.3", {"start": v(822.8, 23.29) * mm, "mid": v(822.11, 21.38) * mm, "end": v(822.82, 19.47) * mm});
            skArc(sketch, "E56.17.0", {"start": v(813.46, 29.68) * mm, "mid": v(813.38, 31.6) * mm, "end": v(811.97, 32.89) * mm});
            skArc(sketch, "E56.17.1", {"start": v(808.77, 31.4) * mm, "mid": v(810.06, 32.8) * mm, "end": v(811.97, 32.89) * mm});
            skArc(sketch, "E56.17.2", {"start": v(808.77, 31.4) * mm, "mid": v(807.46, 29.84) * mm, "end": v(805.45, 29.5) * mm});
            skArc(sketch, "E56.17.3", {"start": v(813.46, 29.68) * mm, "mid": v(813.47, 27.65) * mm, "end": v(814.79, 26.1) * mm});
            skSolve(sketch);
        }
        {
            var Q0;
            Q0 = qSketchRegion(id + "F32", true);
            extrude(context, id + "F33", {"entities" : qUnion([Q0]), "depth" : 5 * mm});
        }
    });
